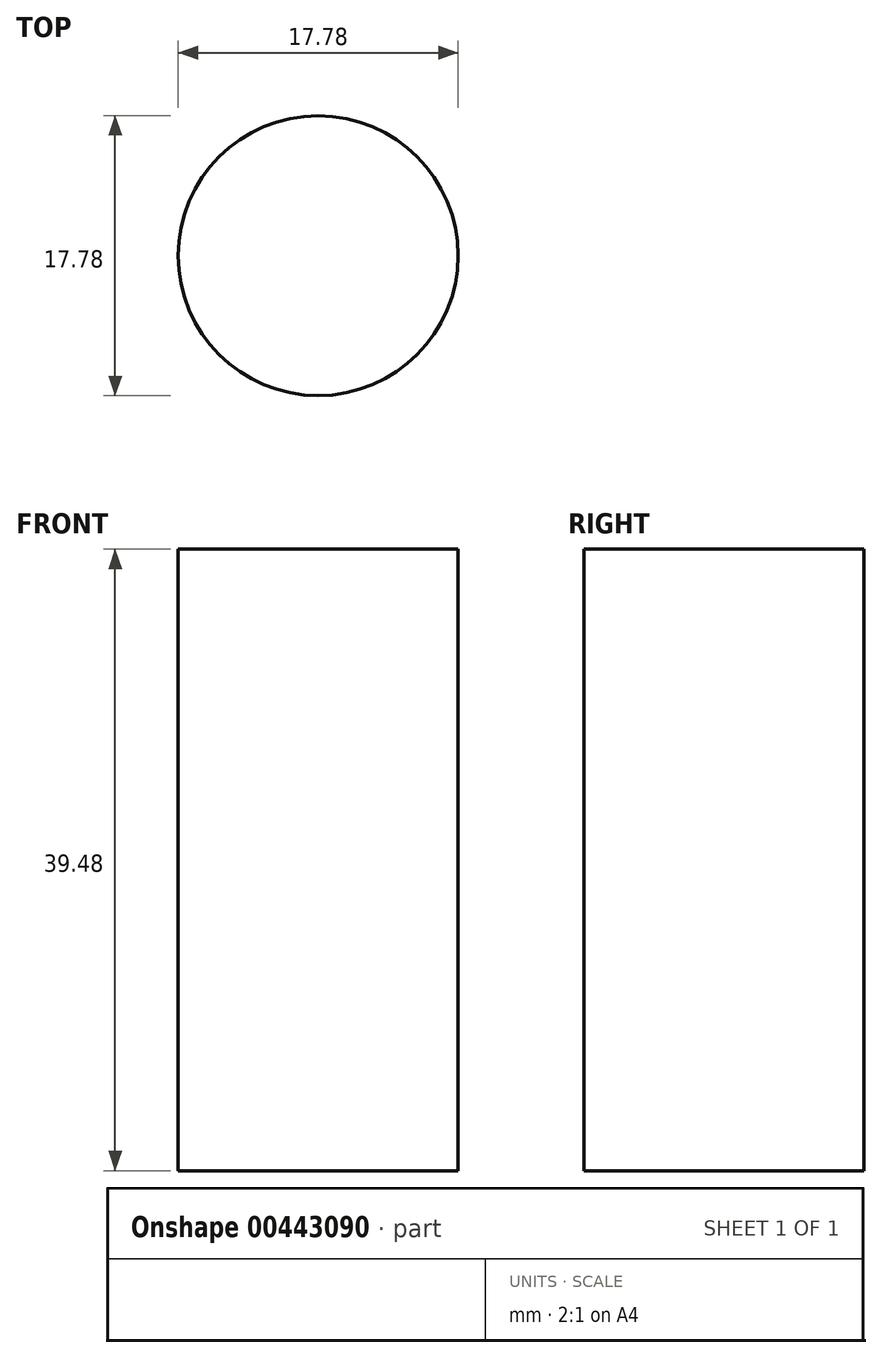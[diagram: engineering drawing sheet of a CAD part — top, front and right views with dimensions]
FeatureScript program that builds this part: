
annotation { "Feature Type Name" : "Feature", "Feature Type Description" : "" }
export const myFeature = defineFeature(function(context is Context, id is Id, definition is map)
    precondition{}
    {
        {
            var Q0;
            Q0=qCreatedBy(makeId("Front.planeOp"),FACE);
            var sketch = newSketch(context, id + "F0", { "sketchPlane" : qUnion([Q0])});
            skLineSegment(sketch, "E0", {"start": v(0, -28.01) * mm, "end": v(-8.89, -28.01) * mm});
            skLineSegment(sketch, "E1", {"start": v(-8.89, -28.01) * mm, "end": v(-8.89, 11.47) * mm});
            skLineSegment(sketch, "E2", {"start": v(-8.89, 11.47) * mm, "end": v(0, 11.47) * mm});
            skLineSegment(sketch, "E3", {"start": v(0, 11.47) * mm, "end": v(0, -28.01) * mm});
            skSolve(sketch);
        }
        {
            var Q0;
            Q0=makeQuery(id+"F0.imprint","IMPRINT",FACE,{"disambiguationData":[TD([[makeQuery(id+"F0.imprint","IMPRINT",EDGE,{"derivedFrom":sQuery(id+"F0.wireOp",EDGE,"E0")}),-1.0]])]});
            var Q1;
            Q1=sQuery(id+"F0.wireOp",EDGE,"E3");
            revolve(context, id + "F1", {"entities" : qUnion([Q0]), "axis" : qUnion([Q1]), "revolveType" : RevolveType.FULL});
        }
    });
